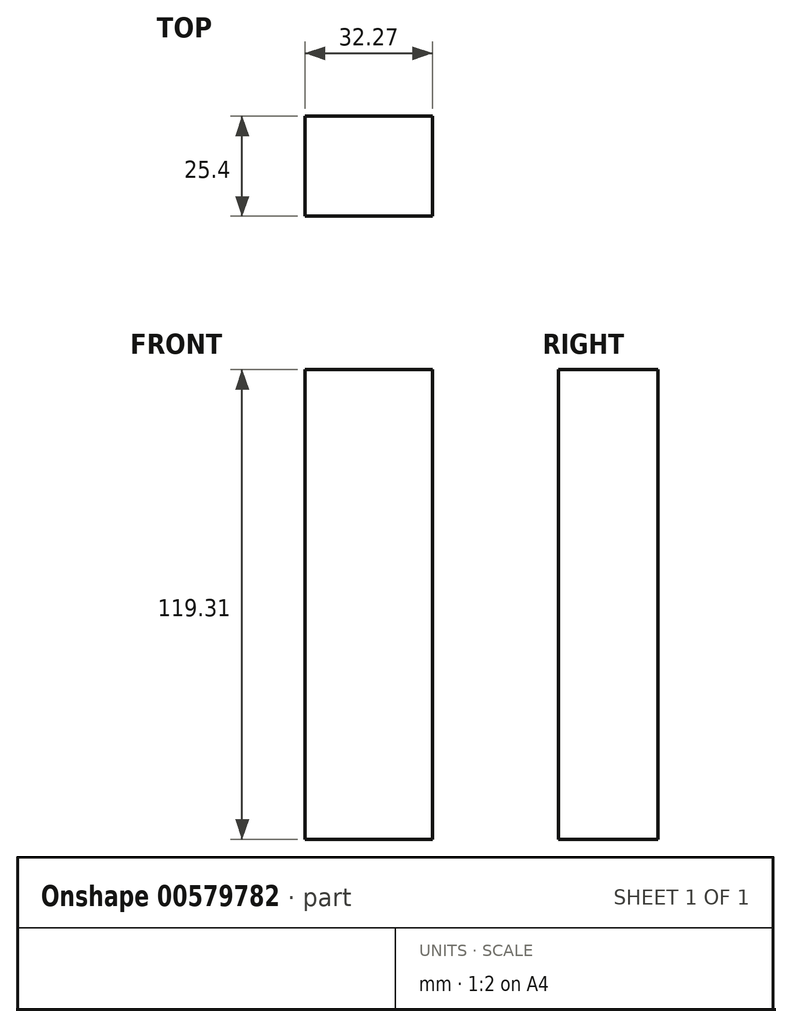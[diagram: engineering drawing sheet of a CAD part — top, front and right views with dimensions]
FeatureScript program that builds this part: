
annotation { "Feature Type Name" : "Feature", "Feature Type Description" : "" }
export const myFeature = defineFeature(function(context is Context, id is Id, definition is map)
    precondition{}
    {
        {
            var Q0;
            Q0=qCreatedBy(makeId("Front.planeOp"),FACE);
            var sketch = newSketch(context, id + "F0", { "sketchPlane" : qUnion([Q0])});
            skLineSegment(sketch, "E0", {"start": v(0, 0) * mm, "end": v(0, 119.3) * mm});
            skLineSegment(sketch, "E1", {"start": v(0, 119.3) * mm, "end": v(-32.27, 119.3) * mm});
            skLineSegment(sketch, "E2", {"start": v(-32.27, 119.3) * mm, "end": v(-32.27, 0) * mm});
            skLineSegment(sketch, "E3", {"start": v(-32.27, 0) * mm, "end": v(0, 0) * mm});
            skSolve(sketch);
        }
        {
            var Q0;
            Q0 = qSketchRegion(id + "F0", true);
            extrude(context, id + "F1", {"entities" : qUnion([Q0]), "depth" : 25.4 * mm, "offsetDistance" : 25.4 * mm});
        }
    });
